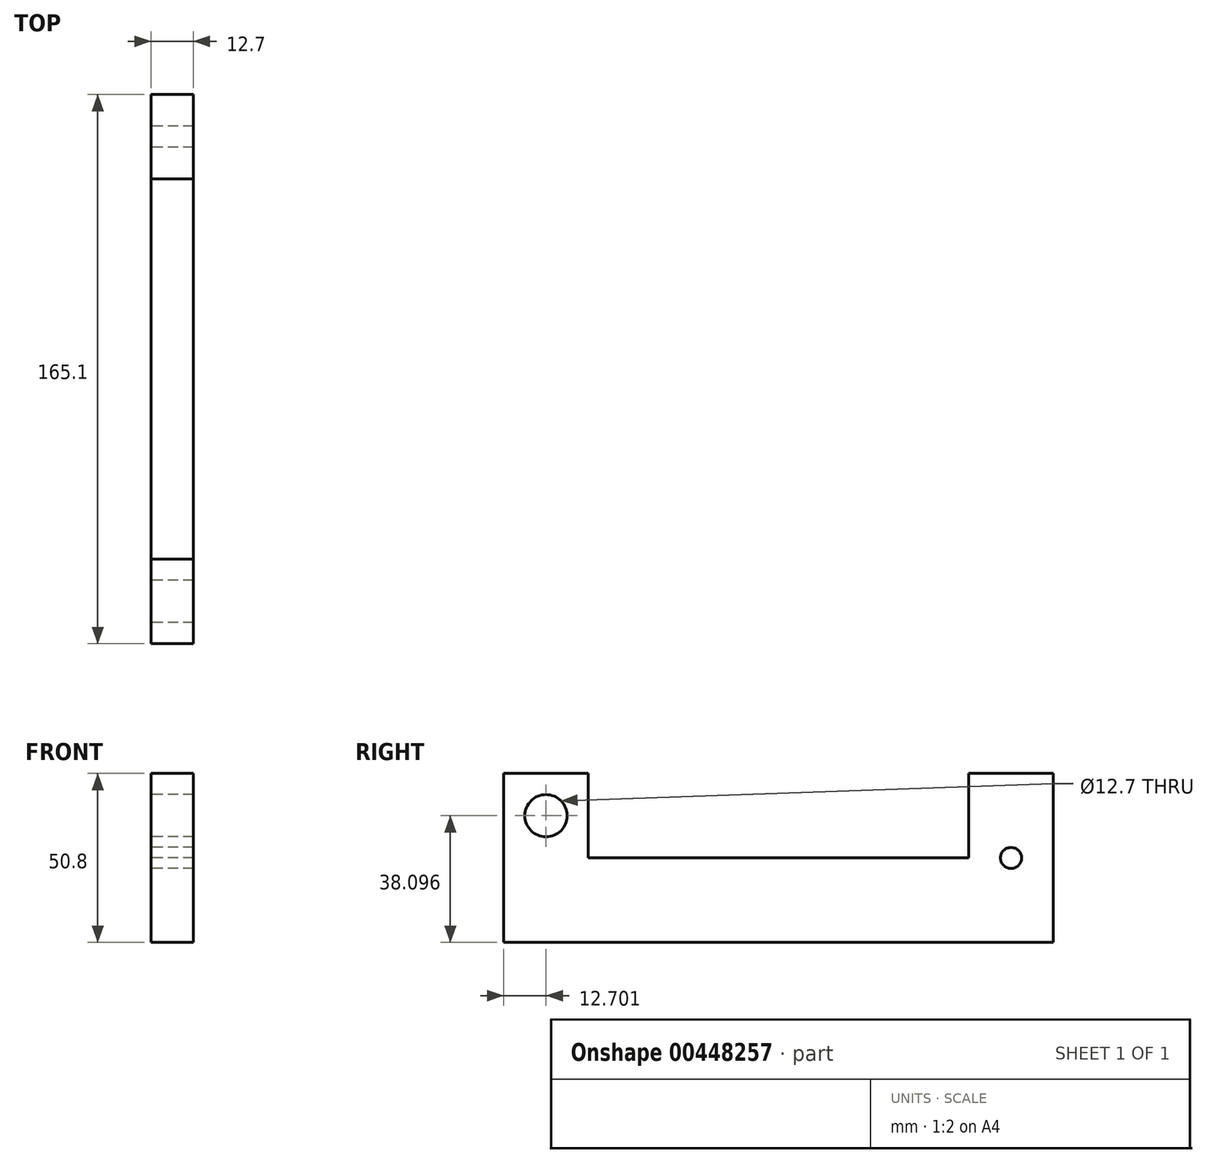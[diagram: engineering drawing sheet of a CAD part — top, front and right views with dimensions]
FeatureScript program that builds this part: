
annotation { "Feature Type Name" : "Feature", "Feature Type Description" : "" }
export const myFeature = defineFeature(function(context is Context, id is Id, definition is map)
    precondition{}
    {
        {
            var Q0;
            Q0=qCreatedBy(makeId("Right.planeOp"),FACE);
            var sketch = newSketch(context, id + "F0", { "sketchPlane" : qUnion([Q0])});
            skLineSegment(sketch, "E0.bottom", {"start": v(-112.69, 13.72) * mm, "end": v(52.41, 13.72) * mm});
            skLineSegment(sketch, "E0.top", {"start": v(-112.69, -37.08) * mm, "end": v(52.41, -37.08) * mm});
            skLineSegment(sketch, "E0.left", {"start": v(-112.69, 13.72) * mm, "end": v(-112.69, -37.08) * mm});
            skLineSegment(sketch, "E0.right", {"start": v(52.41, 13.72) * mm, "end": v(52.41, -37.08) * mm});
            skCircle(sketch, "E1", {"center": v(-99.99, 1.02) * mm, "radius": 6.35 * mm});
            skCircle(sketch, "E2", {"center": v(39.71, -11.68) * mm, "radius": 3.18 * mm});
            skLineSegment(sketch, "E3.bottom", {"start": v(-87.29, 13.72) * mm, "end": v(27.01, 13.72) * mm});
            skLineSegment(sketch, "E3.top", {"start": v(-87.29, -11.68) * mm, "end": v(27.01, -11.68) * mm});
            skLineSegment(sketch, "E3.left", {"start": v(-87.29, 13.72) * mm, "end": v(-87.29, -11.68) * mm});
            skLineSegment(sketch, "E3.right", {"start": v(27.01, 13.72) * mm, "end": v(27.01, -11.68) * mm});
            skSolve(sketch);
        }
        {
            var Q0;
            Q0=makeQuery(id+"F0.imprint","IMPRINT",FACE,{"disambiguationData":[TD([[makeQuery(id+"F0.imprint","IMPRINT",EDGE,{"derivedFrom":sQuery(id+"F0.wireOp",EDGE,"E0.top")}),1.0]])]});
            extrude(context, id + "F1", {"entities" : qUnion([Q0]), "depth" : 12.7 * mm});
        }
    });
